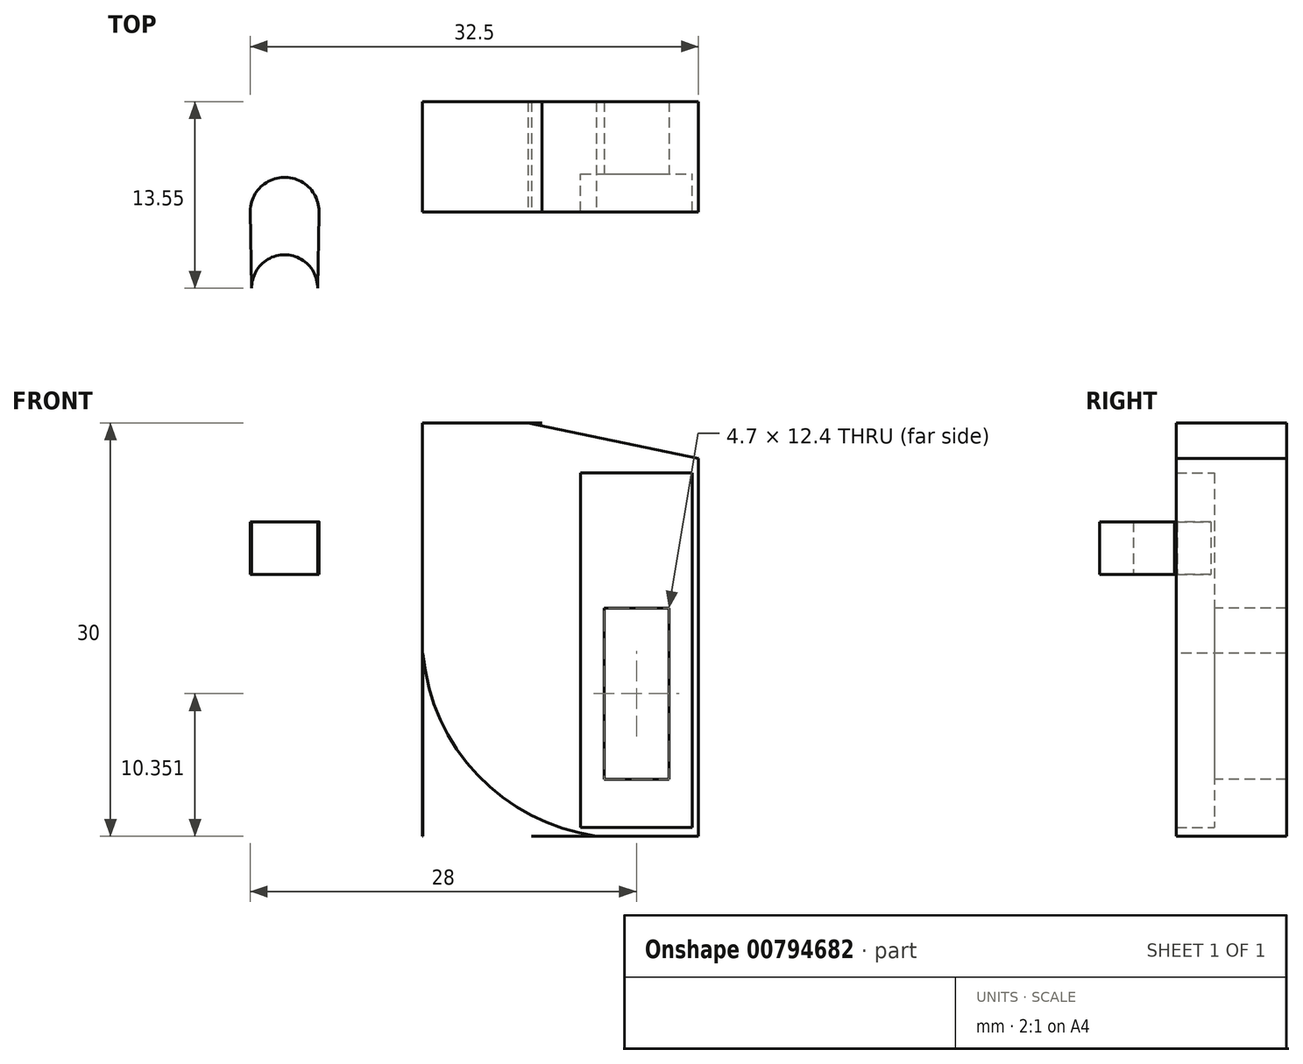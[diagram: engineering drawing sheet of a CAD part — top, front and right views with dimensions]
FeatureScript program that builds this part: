
annotation { "Feature Type Name" : "Feature", "Feature Type Description" : "" }
export const myFeature = defineFeature(function(context is Context, id is Id, definition is map)
    precondition{}
    {
        {
            var Q0;
            Q0=qCreatedBy(makeId("Front.planeOp"),FACE);
            var sketch = newSketch(context, id + "F0", { "sketchPlane" : qUnion([Q0])});
            skLineSegment(sketch, "E0", {"start": v(-49.2, -31.18) * mm, "end": v(-9.2, -31.18) * mm});
            skLineSegment(sketch, "E1", {"start": v(-9.2, -31.18) * mm, "end": v(-9.2, -31.18) * mm});
            skLineSegment(sketch, "E2", {"start": v(-9.2, -31.18) * mm, "end": v(-9.2, -61.18) * mm});
            skLineSegment(sketch, "E3", {"start": v(-9.2, -61.18) * mm, "end": v(-29.2, -61.18) * mm});
            skLineSegment(sketch, "E4", {"start": v(-29.2, -61.18) * mm, "end": v(-29.2, -42.18) * mm});
            skLineSegment(sketch, "E5", {"start": v(-29.2, -42.18) * mm, "end": v(-49.2, -42.18) * mm});
            skLineSegment(sketch, "E6", {"start": v(-49.2, -42.18) * mm, "end": v(-49.2, -31.18) * mm});
            skSolve(sketch);
        }
        {
            var Q0;
            Q0=makeQuery(id+"F0.imprint","IMPRINT",FACE,{"disambiguationData":[TD([[makeQuery(id+"F0.imprint","IMPRINT",EDGE,{"derivedFrom":sQuery(id+"F0.wireOp",EDGE,"E0")}),-1.0]])]});
            extrude(context, id + "F1", {"entities" : qUnion([Q0]), "depth" : 8 * mm, "offsetDistance" : 25 * mm});
        }
        {
            var Q0;
            Q0=makeQuery(id+"F1.opExtrude","CAP_FACE",FACE,{"disambiguationData":[OSD([sQuery(id+"F0.wireOp",EDGE,"E0"),sQuery(id+"F0.wireOp",EDGE,"E1"),sQuery(id+"F0.wireOp",EDGE,"E2"),sQuery(id+"F0.wireOp",EDGE,"E3"),sQuery(id+"F0.wireOp",EDGE,"E4"),sQuery(id+"F0.wireOp",EDGE,"E5"),sQuery(id+"F0.wireOp",EDGE,"E6")])],"isStart":false});
            var sketch = newSketch(context, id + "F2", { "sketchPlane" : qUnion([Q0])});
            skLineSegment(sketch, "E7.bottom", {"start": v(-16.06, -44.63) * mm, "end": v(-11.36, -44.63) * mm});
            skLineSegment(sketch, "E7.top", {"start": v(-16.06, -57.03) * mm, "end": v(-11.36, -57.03) * mm});
            skLineSegment(sketch, "E7.left", {"start": v(-16.06, -44.63) * mm, "end": v(-16.06, -57.03) * mm});
            skLineSegment(sketch, "E7.right", {"start": v(-11.36, -44.63) * mm, "end": v(-11.36, -57.03) * mm});
            skLineSegment(sketch, "E8", {"start": v(-13.7, -31.18) * mm, "end": v(-13.7, -61.18) * mm, "construction": true});
            skSolve(sketch);
        }
        {
            var Q0;
            Q0=makeQuery(id+"F2.imprint","IMPRINT",FACE,{"disambiguationData":[TD([[makeQuery(id+"F2.imprint","IMPRINT",EDGE,{"derivedFrom":sQuery(id+"F2.wireOp",EDGE,"E7.bottom")}),-1.0]])]});
            extrude(context, id + "F3", {"entities" : qUnion([Q0]), "operationType" : NewBodyOperationType.REMOVE, "endBound" : BoundingType.THROUGH_ALL, "oppositeDirection" : true, "depth" : 25 * mm, "offsetDistance" : 25 * mm});
        }
        {
            var Q0;
            Q0=makeQuery(id+"F1.opExtrude","CAP_FACE",FACE,{"disambiguationData":[OSD([sQuery(id+"F0.wireOp",EDGE,"E0"),sQuery(id+"F0.wireOp",EDGE,"E1"),sQuery(id+"F0.wireOp",EDGE,"E2"),sQuery(id+"F0.wireOp",EDGE,"E3"),sQuery(id+"F0.wireOp",EDGE,"E4"),sQuery(id+"F0.wireOp",EDGE,"E5"),sQuery(id+"F0.wireOp",EDGE,"E6")])],"isStart":false});
            var sketch = newSketch(context, id + "F4", { "sketchPlane" : qUnion([Q0])});
            skLineSegment(sketch, "E9.bottom", {"start": v(-17.76, -34.83) * mm, "end": v(-9.66, -34.83) * mm});
            skLineSegment(sketch, "E9.top", {"start": v(-17.76, -60.53) * mm, "end": v(-9.66, -60.53) * mm});
            skLineSegment(sketch, "E9.left", {"start": v(-17.76, -34.83) * mm, "end": v(-17.76, -60.53) * mm});
            skLineSegment(sketch, "E9.right", {"start": v(-9.66, -34.83) * mm, "end": v(-9.66, -60.53) * mm});
            skLineSegment(sketch, "E10", {"start": v(-13.7, -31.18) * mm, "end": v(-13.7, -61.18) * mm, "construction": true});
            skSolve(sketch);
        }
        {
            var Q0;
            {var subQ1=sQuery(id+"F4.wireOp",EDGE,"E9.bottom");Q0=makeQuery(id+"F4.imprint","IMPRINT",FACE,{"disambiguationData":[TD([[makeQuery(id+"F4.imprint","IMPRINT",EDGE,{"derivedFrom":subQ1}),-1.0]])]});}
            extrude(context, id + "F5", {"entities" : qUnion([Q0]), "operationType" : NewBodyOperationType.REMOVE, "endBound" : BoundingType.SYMMETRIC, "depth" : 5.5 * mm, "offsetDistance" : 25 * mm});
        }
        {
            var Q0;
            Q0=makeQuery(id+"F1.opExtrude","SWEPT_FACE",FACE,{"disambiguationData":[OSD([sQuery(id+"F0.wireOp",EDGE,"E5")])]});
            var sketch = newSketch(context, id + "F6", { "sketchPlane" : qUnion([Q0])});
            skLineSegment(sketch, "E11.bottom", {"start": v(-49.2, 3) * mm, "end": v(-29.2, 3) * mm});
            skLineSegment(sketch, "E11.top", {"start": v(-49.2, 8) * mm, "end": v(-29.2, 8) * mm});
            skLineSegment(sketch, "E11.left", {"start": v(-49.2, 3) * mm, "end": v(-49.2, 8) * mm});
            skLineSegment(sketch, "E11.right", {"start": v(-29.2, 3) * mm, "end": v(-29.2, 8) * mm});
            skSolve(sketch);
        }
        {
            var Q0;
            Q0=makeQuery(id+"F6.imprint","IMPRINT",FACE,{"disambiguationData":[TD([[makeQuery(id+"F6.imprint","IMPRINT",EDGE,{"derivedFrom":sQuery(id+"F6.wireOp",EDGE,"E11.bottom")}),1.0]])]});
            extrude(context, id + "F7", {"entities" : qUnion([Q0]), "operationType" : NewBodyOperationType.REMOVE, "endBound" : BoundingType.THROUGH_ALL, "oppositeDirection" : true, "depth" : 25 * mm, "offsetDistance" : 25 * mm});
        }
        {
            var Q0;
            Q0=makeQuery(id+"F7.boolean.opBoolean","COPY",FACE,{"derivedFrom":makeQuery(id+"F7.opExtrude","SWEPT_FACE",FACE,{"disambiguationData":[OSD([sQuery(id+"F6.wireOp",EDGE,"E11.bottom")])]})});
            var sketch = newSketch(context, id + "F8", { "sketchPlane" : qUnion([Q0])});
            skLineSegment(sketch, "E12.bottom", {"start": v(-29.3, -38.36) * mm, "end": v(-49.3, -38.36) * mm});
            skLineSegment(sketch, "E12.top", {"start": v(-29.3, -42.36) * mm, "end": v(-49.3, -42.36) * mm});
            skLineSegment(sketch, "E12.left", {"start": v(-29.3, -38.36) * mm, "end": v(-29.3, -42.36) * mm});
            skLineSegment(sketch, "E12.right", {"start": v(-49.3, -38.36) * mm, "end": v(-49.3, -42.36) * mm});
            skSolve(sketch);
        }
        {
            var Q0;
            {var subQ0=sQuery(id+"F8.wireOp",EDGE,"E12.left");var subQ1=sQuery(id+"F8.wireOp",EDGE,"E12.bottom");var subQ2=makeQuery(id+"F8.imprint","INTERSECT",VERTEX,{"derivedFrom":[subQ1,subQ0]});Q0=makeQuery(id+"F8.imprint","IMPRINT",FACE,{"disambiguationData":[TD([[makeQuery(id+"F8.imprint","IMPRINT",EDGE,{"disambiguationData":[TD([[subQ2,-1.0]])],"derivedFrom":subQ0}),-1.0]])]});}
            extrude(context, id + "F9", {"entities" : qUnion([Q0]), "operationType" : NewBodyOperationType.ADD, "depth" : 15 * mm, "offsetDistance" : 25 * mm});
        }
        {
            var Q0;
            Q0=makeQuery(id+"F9.boolean.opBoolean","MERGE",FACE,{"derivedFrom":[makeQuery(id+"F1.opExtrude","SWEPT_FACE",FACE,{"disambiguationData":[OSD([sQuery(id+"F0.wireOp",EDGE,"E5")])]}),makeQuery(id+"F9.opExtrude","SWEPT_FACE",FACE,{"disambiguationData":[OSD([sQuery(id+"F6.wireOp",EDGE,"E11.bottom")])]})]});
            var sketch = newSketch(context, id + "F10", { "sketchPlane" : qUnion([Q0])});
            skCircle(sketch, "E13", {"center": v(-39.2, 8) * mm, "radius": 2.5 * mm});
            skCircle(sketch, "E14", {"center": v(-39.2, 13.5) * mm, "radius": 2.39 * mm});
            skLineSegment(sketch, "E15", {"start": v(-36.71, 7.98) * mm, "end": v(-36.82, 13.55) * mm});
            skLineSegment(sketch, "E16", {"start": v(-41.7, 7.94) * mm, "end": v(-41.6, 13.55) * mm});
            skSolve(sketch);
        }
        {
            var Q0;
            {var subQ0=sQuery(id+"F10.wireOp",EDGE,"E14");var subQ1=makeQuery(id+"F10.imprint","INTERSECT",VERTEX,{"derivedFrom":[subQ0,sQuery(id+"F10.wireOp",EDGE,"E15")]});Q0=makeQuery(id+"F10.imprint","IMPRINT",FACE,{"disambiguationData":[TD([[makeQuery(id+"F10.imprint","IMPRINT",EDGE,{"disambiguationData":[TD([[subQ1,-1.0]])],"derivedFrom":subQ0}),1.0]])]});}
            var Q1;
            {var subQ0=sQuery(id+"F10.wireOp",EDGE,"E16");var subQ1=sQuery(id+"F10.wireOp",EDGE,"E13");var subQ2=makeQuery(id+"F10.imprint","INTERSECT",VERTEX,{"disambiguationData":[OD(1.0)],"derivedFrom":[subQ1,subQ0]});Q1=makeQuery(id+"F10.imprint","IMPRINT",FACE,{"disambiguationData":[TD([[makeQuery(id+"F10.imprint","IMPRINT",EDGE,{"disambiguationData":[TD([[subQ2,1.0]])],"derivedFrom":subQ1}),1.0]])]});}
            var Q2;
            {var subQ0=sQuery(id+"F10.wireOp",EDGE,"E16");var subQ1=sQuery(id+"F10.wireOp",EDGE,"E13");var subQ2=makeQuery(id+"F10.imprint","INTERSECT",VERTEX,{"disambiguationData":[OD(1.0)],"derivedFrom":[subQ1,subQ0]});Q2=makeQuery(id+"F10.imprint","IMPRINT",FACE,{"disambiguationData":[TD([[makeQuery(id+"F10.imprint","IMPRINT",EDGE,{"disambiguationData":[TD([[subQ2,1.0]])],"derivedFrom":subQ1}),-1.0]])]});}
            var Q3;
            Q3=sQuery(id+"F10.wireOp",EDGE,"E14");
            var Q4;
            Q4=sQuery(id+"F10.wireOp",EDGE,"E13");
            var Q5;
            Q5=sQuery(id+"F10.wireOp",EDGE,"E15");
            var Q6;
            Q6=sQuery(id+"F10.wireOp",EDGE,"E16");
            extrude(context, id + "F11", {"entities" : qUnion([Q0, Q1, Q2]), "operationType" : NewBodyOperationType.REMOVE, "surfaceEntities" : qUnion([Q3, Q4, Q5, Q6]), "endBound" : BoundingType.THROUGH_ALL, "oppositeDirection" : true, "depth" : 25 * mm, "offsetDistance" : 25 * mm});
        }
        {
            var Q0;
            Q0=makeQuery(id+"F2.imprint","IMPRINT",FACE,{"disambiguationData":[TD([[makeQuery(id+"F2.imprint","IMPRINT",EDGE,{"derivedFrom":sQuery(id+"F2.wireOp",EDGE,"E7.bottom")}),1.0]])]});
            var sketch = newSketch(context, id + "F12", { "sketchPlane" : qUnion([Q0])});
            skLineSegment(sketch, "E17", {"start": v(-49.22, -31.24) * mm, "end": v(-49.22, -34.49) * mm});
            skLineSegment(sketch, "E18", {"start": v(-45.6, -31.17) * mm, "end": v(-49.22, -34.49) * mm});
            skSolve(sketch);
        }
        {
            var Q0;
            {var subQ0=sQuery(id+"F12.wireOp",EDGE,"E18");var subQ1=makeQuery(id+"F2.imprint","IMPRINT",EDGE,{"derivedFrom":makeQuery(id+"F1.opExtrude","CAP_EDGE",EDGE,{"disambiguationData":[OSD([sQuery(id+"F0.wireOp",EDGE,"E0")])],"isStart":false})});var subQ2=makeQuery(id+"F12.imprint","INTERSECT",VERTEX,{"derivedFrom":[subQ1,subQ0]});Q0=makeQuery(id+"F12.imprint","IMPRINT",FACE,{"disambiguationData":[TD([[makeQuery(id+"F12.imprint","IMPRINT",EDGE,{"disambiguationData":[TD([[subQ2,-1.0]])],"derivedFrom":subQ0}),-1.0]])]});}
            extrude(context, id + "F13", {"entities" : qUnion([Q0]), "operationType" : NewBodyOperationType.REMOVE, "endBound" : BoundingType.THROUGH_ALL, "oppositeDirection" : true, "depth" : 25 * mm, "offsetDistance" : 25 * mm});
        }
        {
            var Q0;
            Q0=makeQuery(id+"F2.imprint","IMPRINT",FACE,{"disambiguationData":[TD([[makeQuery(id+"F2.imprint","IMPRINT",EDGE,{"derivedFrom":sQuery(id+"F2.wireOp",EDGE,"E7.bottom")}),1.0]])]});
            var sketch = newSketch(context, id + "F14", { "sketchPlane" : qUnion([Q0])});
            skArc(sketch, "E19", {"start": v(-29.18, -47.9) * mm, "mid": v(-25.22, -56.73) * mm, "end": v(-16.61, -61.15) * mm});
            skLineSegment(sketch, "E20", {"start": v(-29.18, -47.9) * mm, "end": v(-29.18, -61.23) * mm});
            skLineSegment(sketch, "E21", {"start": v(-29.18, -61.23) * mm, "end": v(-16.61, -61.15) * mm});
            skSolve(sketch);
        }
        {
            var Q0;
            Q0 = qSketchRegion(id + "F14", true);
            extrude(context, id + "F15", {"entities" : qUnion([Q0]), "operationType" : NewBodyOperationType.REMOVE, "endBound" : BoundingType.THROUGH_ALL, "oppositeDirection" : true, "depth" : 25 * mm, "offsetDistance" : 25 * mm});
        }
        {
            var Q0;
            Q0=makeQuery(id+"F4.imprint","IMPRINT",FACE,{"disambiguationData":[TD([[makeQuery(id+"F4.imprint","IMPRINT",EDGE,{"derivedFrom":sQuery(id+"F4.wireOp",EDGE,"E9.bottom")}),1.0]])]});
            var sketch = newSketch(context, id + "F16", { "sketchPlane" : qUnion([Q0])});
            skLineSegment(sketch, "E22", {"start": v(-21.56, -31.19) * mm, "end": v(-9.07, -33.79) * mm});
            skLineSegment(sketch, "E23", {"start": v(-9.07, -33.79) * mm, "end": v(-9.07, -31.09) * mm});
            skLineSegment(sketch, "E24", {"start": v(-9.07, -31.09) * mm, "end": v(-21.56, -31.19) * mm});
            skSolve(sketch);
        }
        {
            var Q0;
            Q0 = qSketchRegion(id + "F16", true);
            extrude(context, id + "F17", {"entities" : qUnion([Q0]), "operationType" : NewBodyOperationType.REMOVE, "endBound" : BoundingType.THROUGH_ALL, "oppositeDirection" : true, "depth" : 25 * mm, "offsetDistance" : 25 * mm});
        }
    });
